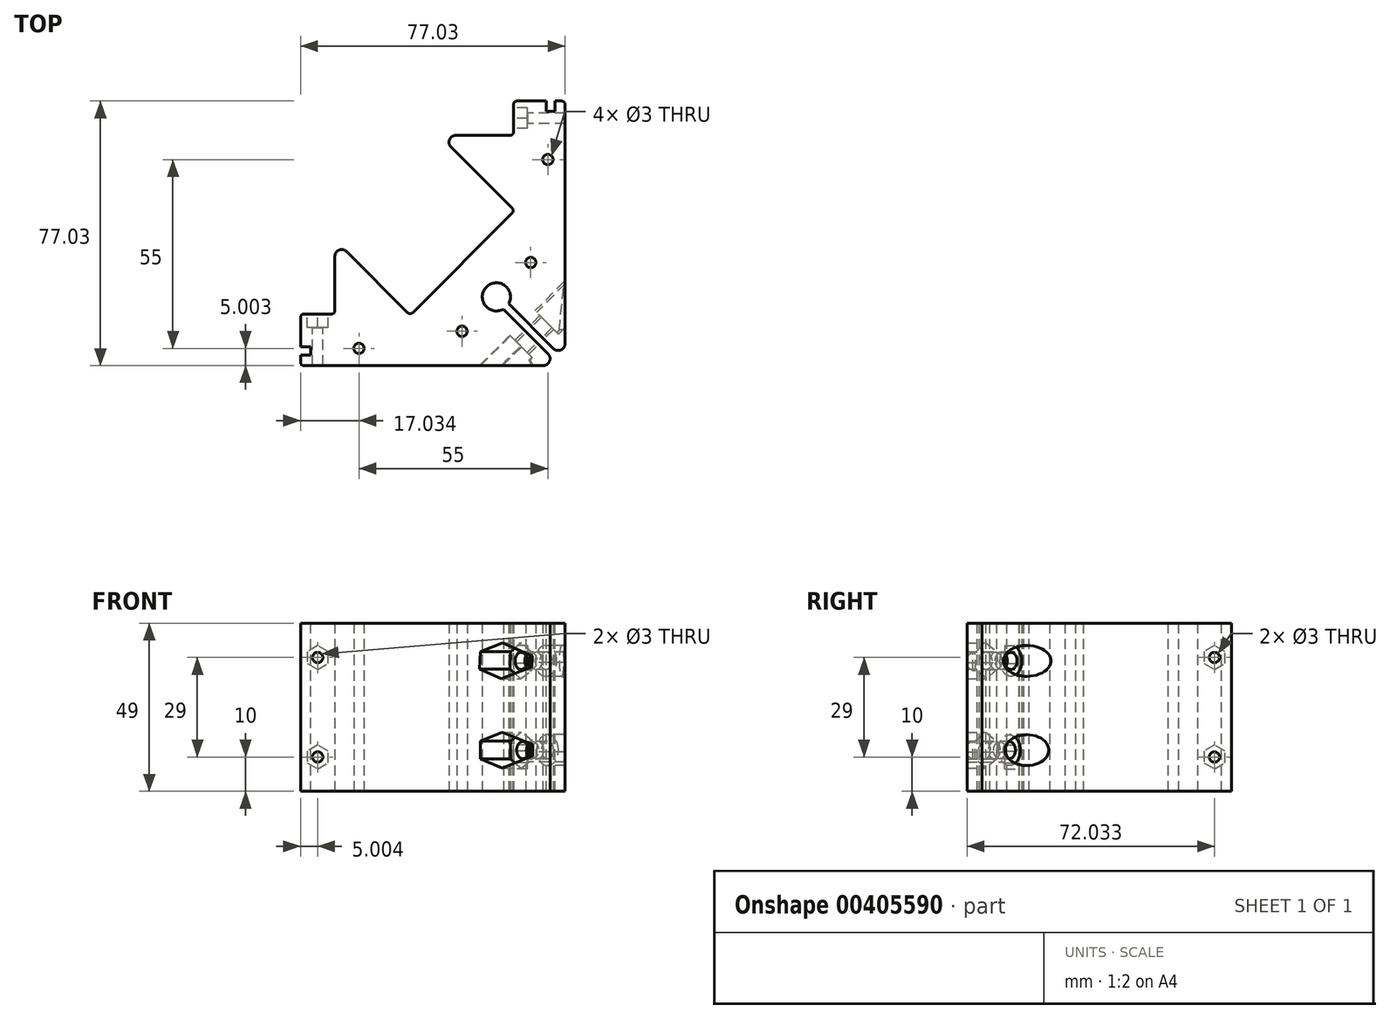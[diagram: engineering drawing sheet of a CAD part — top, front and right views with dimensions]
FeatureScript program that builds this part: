
annotation { "Feature Type Name" : "Feature", "Feature Type Description" : "" }
export const myFeature = defineFeature(function(context is Context, id is Id, definition is map)
    precondition{}
    {
        {
            var Q0;
            Q0=qCreatedBy(makeId("Top.planeOp"),FACE);
            var sketch = newSketch(context, id + "F0", { "sketchPlane" : qUnion([Q0])});
            skLineSegment(sketch, "E0.top", {"start": v(-78.82, 0.93) * mm, "end": v(-4.07, 0.93) * mm});
            skLineSegment(sketch, "E0.right", {"start": v(-1.79, 77.96) * mm, "end": v(-1.79, 3.21) * mm});
            skLineSegment(sketch, "E1", {"start": v(-18.22, 18.92) * mm, "end": v(-2.3, 3) * mm});
            skLineSegment(sketch, "E2.MirrorCS", {"start": v(-19.77, 17.36) * mm, "end": v(-3.85, 1.44) * mm});
            skPoint(sketch, "E3.visualSharp", {"position": v(-1.79, 2.49) * mm});
            skPoint(sketch, "E4.visualSharp", {"position": v(-3.34, 0.93) * mm});
            skPoint(sketch, "E5", {"position": v(-46.54, 45.68) * mm});
            skLineSegment(sketch, "E6", {"start": v(-31.69, 30.83) * mm, "end": v(-46.54, 15.98) * mm});
            skLineSegment(sketch, "E7", {"start": v(-31.69, 30.83) * mm, "end": v(-16.84, 45.68) * mm});
            skLineSegment(sketch, "E8", {"start": v(-1.79, 77.96) * mm, "end": v(-16.79, 77.96) * mm});
            skLineSegment(sketch, "E9", {"start": v(-78.82, 0.93) * mm, "end": v(-78.82, 15.93) * mm});
            skPoint(sketch, "E10.orphan", {"position": v(-49.12, 77.96) * mm});
            skLineSegment(sketch, "E11", {"start": v(-68.82, 36.93) * mm, "end": v(-68.82, 15.93) * mm});
            skLineSegment(sketch, "E12", {"start": v(-68.82, 15.93) * mm, "end": v(-78.82, 15.93) * mm});
            skLineSegment(sketch, "E13.top", {"start": v(-37.79, 67.96) * mm, "end": v(-16.79, 67.96) * mm});
            skLineSegment(sketch, "E13.right", {"start": v(-16.79, 77.96) * mm, "end": v(-16.79, 67.96) * mm});
            skArc(sketch, "E14", {"start": v(-18.22, 18.92) * mm, "mid": v(-24.69, 23.83) * mm, "end": v(-19.77, 17.36) * mm});
            skLineSegment(sketch, "E15", {"start": v(-3.85, 1.44) * mm, "end": v(-3.34, 0.93) * mm});
            skLineSegment(sketch, "E16", {"start": v(-4.07, 0.93) * mm, "end": v(-3.34, 0.93) * mm});
            skLineSegment(sketch, "E17", {"start": v(-1.79, 2.49) * mm, "end": v(-1.79, 3.21) * mm});
            skLineSegment(sketch, "E18", {"start": v(-2.3, 3) * mm, "end": v(-1.79, 2.49) * mm});
            skLineSegment(sketch, "E19", {"start": v(-46.54, 15.98) * mm, "end": v(-12.5, 50.02) * mm});
            skLineSegment(sketch, "E20", {"start": v(-16.48, 46.04) * mm, "end": v(-46.89, 15.63) * mm});
            skLineSegment(sketch, "E21", {"start": v(-16.48, 46.04) * mm, "end": v(-37.79, 67.34) * mm});
            skLineSegment(sketch, "E22", {"start": v(-46.89, 15.63) * mm, "end": v(-68.2, 36.93) * mm});
            skLineSegment(sketch, "E23", {"start": v(-68.2, 36.93) * mm, "end": v(-68.82, 37.56) * mm});
            skLineSegment(sketch, "E24", {"start": v(-68.82, 37.56) * mm, "end": v(-68.82, 36.93) * mm});
            skLineSegment(sketch, "E25", {"start": v(-37.79, 67.96) * mm, "end": v(-38.41, 67.96) * mm});
            skLineSegment(sketch, "E26", {"start": v(-37.79, 67.34) * mm, "end": v(-38.41, 67.96) * mm});
            skSolve(sketch);
        }
        {
            var Q0;
            Q0=qSketchRegion(id+"F0",true);
            extrude(context, id + "F1", {"entities" : qUnion([Q0]), "depth" : 49 * mm});
        }
        {
            var Q0;
            Q0=makeQuery(id+"F1.opExtrude","SWEPT_FACE",FACE,{"disambiguationData":[OSD([sQuery(id+"F0.wireOp",EDGE,"E1")])]});
            var sketch = newSketch(context, id + "F2", { "sketchPlane" : qUnion([Q0])});
            skCircle(sketch, "E27", {"center": v(-14.26, 12) * mm, "radius": 2.5 * mm});
            skCircle(sketch, "E28", {"center": v(-14.92, 38) * mm, "radius": 4.5 * mm});
            skCircle(sketch, "E29", {"center": v(-14.26, 12) * mm, "radius": 4.5 * mm});
            skCircle(sketch, "E30", {"center": v(-14.92, 38) * mm, "radius": 2.5 * mm});
            skCircle(sketch, "E31.cCircle", {"center": v(-14.92, 38) * mm, "radius": 4.5 * mm, "construction": true});
            skLineSegment(sketch, "E31.0", {"start": v(-10.5, 35.26) * mm, "end": v(-15.08, 32.8) * mm});
            skLineSegment(sketch, "E31.1", {"start": v(-15.08, 32.8) * mm, "end": v(-19.5, 35.54) * mm});
            skLineSegment(sketch, "E31.2", {"start": v(-19.5, 35.54) * mm, "end": v(-19.34, 40.74) * mm});
            skLineSegment(sketch, "E31.3", {"start": v(-19.34, 40.74) * mm, "end": v(-14.76, 43.2) * mm});
            skLineSegment(sketch, "E31.4", {"start": v(-14.76, 43.2) * mm, "end": v(-10.34, 40.46) * mm});
            skLineSegment(sketch, "E31.5", {"start": v(-10.34, 40.46) * mm, "end": v(-10.5, 35.26) * mm});
            skPoint(sketch, "E31.0.midPoint", {"position": v(-12.79, 34.04) * mm});
            skSolve(sketch);
        }
        {
            var Q0;
            Q0=sQuery(id+"F2.wireOp",VERTEX,"E28.center");
            var Q1;
            Q1=makeQuery(id+"F1.opExtrude","SWEPT_BODY",BODY,{"disambiguationData":[OSD([sQuery(id+"F0.wireOp",EDGE,"E0.bottom"),sQuery(id+"F0.wireOp",EDGE,"E0.top"),sQuery(id+"F0.wireOp",EDGE,"E0.left"),sQuery(id+"F0.wireOp",EDGE,"E0.right"),sQuery(id+"F0.wireOp",EDGE,"qFsGaKan-yORc-CTVH-xqod-amC7XaK1J5uG"),sQuery(id+"F0.wireOp",EDGE,"E1"),sQuery(id+"F0.wireOp",EDGE,"E2.MirrorCS"),sQuery(id+"F0.wireOp",EDGE,"cd217c19-c853-48cb-b8bd-9b78fb10cb74.filletArc"),sQuery(id+"F0.wireOp",EDGE,"a7c015ec-a513-4ea6-9d75-b2fe8166aac2.filletArc"),sQuery(id+"F0.wireOp",EDGE,"E3.filletArc"),sQuery(id+"F0.wireOp",EDGE,"E4.filletArc")])]});
            hole(context, id + "F3", {"style" : HoleStyle.SIMPLE, "endStyle" : HoleEndStyle.THROUGH, "holeDiameter" : 5 * mm, "isTappedThrough" : true, "tappedDepth" : 12 * mm, "tapClearance" : 3, "locations" : qUnion([Q0]), "scope" : qUnion([Q1])});
        }
        {
            var Q0;
            Q0=sQuery(id+"F2.wireOp",VERTEX,"E28.center");
            var Q1;
            Q1=makeQuery(id+"F1.opExtrude","SWEPT_BODY",BODY,{"disambiguationData":[OSD([sQuery(id+"F0.wireOp",EDGE,"E0.bottom"),sQuery(id+"F0.wireOp",EDGE,"E0.top"),sQuery(id+"F0.wireOp",EDGE,"E0.left"),sQuery(id+"F0.wireOp",EDGE,"E0.right"),sQuery(id+"F0.wireOp",EDGE,"qFsGaKan-yORc-CTVH-xqod-amC7XaK1J5uG"),sQuery(id+"F0.wireOp",EDGE,"E1"),sQuery(id+"F0.wireOp",EDGE,"E2.MirrorCS"),sQuery(id+"F0.wireOp",EDGE,"cd217c19-c853-48cb-b8bd-9b78fb10cb74.filletArc"),sQuery(id+"F0.wireOp",EDGE,"a7c015ec-a513-4ea6-9d75-b2fe8166aac2.filletArc"),sQuery(id+"F0.wireOp",EDGE,"E3.filletArc"),sQuery(id+"F0.wireOp",EDGE,"E4.filletArc")])]});
            hole(context, id + "F4", {"style" : HoleStyle.SIMPLE, "endStyle" : HoleEndStyle.THROUGH, "oppositeDirection" : true, "standardTappedOrClearance" : lookupTablePath({ "standard" : "自訂" }), "standardBlindInLast" : lookupTablePath({ "standard" : "自訂" }), "holeDiameter" : 5 * mm, "isTappedThrough" : true, "tappedDepth" : 12 * mm, "tapClearance" : 3, "locations" : qUnion([Q0]), "scope" : qUnion([Q1])});
        }
        {
            var Q0;
            Q0=makeQuery(id+"F2.imprint","IMPRINT",FACE,{"disambiguationData":[TD([[makeQuery(id+"F2.imprint","IMPRINT",EDGE,{"derivedFrom":sQuery(id+"F2.wireOp",EDGE,"E28")}),1.0]])]});
            var Q1;
            Q1=sQuery(id+"F2.wireOp",EDGE,"E28");
            extrude(context, id + "F5", {"entities" : qUnion([Q0]), "surfaceEntities" : qUnion([Q1]), "oppositeDirection" : true, "depth" : 25 * mm});
        }
        {
            var Q0;
            Q0=makeQuery(id+"F5.opExtrude","SWEPT_BODY",BODY,{"disambiguationData":[OSD([sQuery(id+"F2.wireOp",EDGE,"E28"),sQuery(id+"F2.wireOp",EDGE,"E30")])]});
            var Q1;
            Q1=makeQuery(id+"F1.opExtrude","SWEPT_BODY",BODY,{"disambiguationData":[OSD([sQuery(id+"F0.wireOp",EDGE,"E0.bottom"),sQuery(id+"F0.wireOp",EDGE,"E0.top"),sQuery(id+"F0.wireOp",EDGE,"E0.left"),sQuery(id+"F0.wireOp",EDGE,"E0.right"),sQuery(id+"F0.wireOp",EDGE,"qFsGaKan-yORc-CTVH-xqod-amC7XaK1J5uG"),sQuery(id+"F0.wireOp",EDGE,"E1"),sQuery(id+"F0.wireOp",EDGE,"E2.MirrorCS"),sQuery(id+"F0.wireOp",EDGE,"cd217c19-c853-48cb-b8bd-9b78fb10cb74.filletArc"),sQuery(id+"F0.wireOp",EDGE,"a7c015ec-a513-4ea6-9d75-b2fe8166aac2.filletArc"),sQuery(id+"F0.wireOp",EDGE,"E3.filletArc"),sQuery(id+"F0.wireOp",EDGE,"E4.filletArc")])]});
            booleanBodies(context, id + "F6", {"operationType" : BooleanOperationType.SUBTRACTION, "tools" : qUnion([Q0]), "targets" : qUnion([Q1])});
        }
        {
            var Q0;
            Q0=makeQuery(id+"F2.imprint","IMPRINT",FACE,{"disambiguationData":[TD([[makeQuery(id+"F2.imprint","IMPRINT",EDGE,{"derivedFrom":sQuery(id+"F2.wireOp",EDGE,"E28")}),1.0]])]});
            extrude(context, id + "F7", {"entities" : qUnion([Q0]), "operationType" : NewBodyOperationType.ADD, "oppositeDirection" : true, "depth" : 4 * mm});
        }
        {
            var Q0;
            Q0=sQuery(id+"F2.wireOp",VERTEX,"E27.center");
            var Q1;
            Q1=makeQuery(id+"F1.opExtrude","SWEPT_BODY",BODY,{"disambiguationData":[OSD([sQuery(id+"F0.wireOp",EDGE,"E0.bottom"),sQuery(id+"F0.wireOp",EDGE,"E0.top"),sQuery(id+"F0.wireOp",EDGE,"E0.left"),sQuery(id+"F0.wireOp",EDGE,"E0.right"),sQuery(id+"F0.wireOp",EDGE,"qFsGaKan-yORc-CTVH-xqod-amC7XaK1J5uG"),sQuery(id+"F0.wireOp",EDGE,"E1"),sQuery(id+"F0.wireOp",EDGE,"E2.MirrorCS"),sQuery(id+"F0.wireOp",EDGE,"cd217c19-c853-48cb-b8bd-9b78fb10cb74.filletArc"),sQuery(id+"F0.wireOp",EDGE,"a7c015ec-a513-4ea6-9d75-b2fe8166aac2.filletArc"),sQuery(id+"F0.wireOp",EDGE,"E3.filletArc"),sQuery(id+"F0.wireOp",EDGE,"E4.filletArc")])]});
            hole(context, id + "F8", {"style" : HoleStyle.SIMPLE, "endStyle" : HoleEndStyle.THROUGH, "oppositeDirection" : true, "standardTappedOrClearance" : lookupTablePath({ "standard" : "自訂" }), "standardBlindInLast" : lookupTablePath({ "standard" : "自訂" }), "holeDiameter" : 5 * mm, "isTappedThrough" : true, "tappedDepth" : 12 * mm, "tapClearance" : 3, "locations" : qUnion([Q0]), "scope" : qUnion([Q1])});
        }
        {
            var Q0;
            Q0=makeQuery(id+"F1.opExtrude","SWEPT_FACE",FACE,{"disambiguationData":[OSD([sQuery(id+"F0.wireOp",EDGE,"E2.MirrorCS")])]});
            var sketch = newSketch(context, id + "F9", { "sketchPlane" : qUnion([Q0])});
            skCircle(sketch, "E32.cCircle", {"center": v(14.92, 38) * mm, "radius": 4.5 * mm, "construction": true});
            skLineSegment(sketch, "E32.0", {"start": v(10.34, 40.45) * mm, "end": v(14.75, 43.2) * mm});
            skLineSegment(sketch, "E32.1", {"start": v(14.75, 43.2) * mm, "end": v(19.33, 40.74) * mm});
            skLineSegment(sketch, "E32.2", {"start": v(19.33, 40.74) * mm, "end": v(19.5, 35.55) * mm});
            skLineSegment(sketch, "E32.3", {"start": v(19.5, 35.55) * mm, "end": v(15.08, 32.8) * mm});
            skLineSegment(sketch, "E32.4", {"start": v(15.08, 32.8) * mm, "end": v(10.5, 35.26) * mm});
            skLineSegment(sketch, "E32.5", {"start": v(10.5, 35.26) * mm, "end": v(10.34, 40.45) * mm});
            skPoint(sketch, "E32.0.midPoint", {"position": v(12.54, 41.82) * mm});
            skCircle(sketch, "E33", {"center": v(14.92, 38) * mm, "radius": 2.5 * mm});
            skCircle(sketch, "E34.cCircle", {"center": v(14.82, 12) * mm, "radius": 4.5 * mm, "construction": true});
            skLineSegment(sketch, "E34.0", {"start": v(19.32, 14.6) * mm, "end": v(19.32, 9.4) * mm});
            skLineSegment(sketch, "E34.1", {"start": v(19.32, 9.4) * mm, "end": v(14.82, 6.8) * mm});
            skLineSegment(sketch, "E34.2", {"start": v(14.82, 6.8) * mm, "end": v(10.32, 9.4) * mm});
            skLineSegment(sketch, "E34.3", {"start": v(10.32, 9.4) * mm, "end": v(10.32, 14.6) * mm});
            skLineSegment(sketch, "E34.4", {"start": v(10.32, 14.6) * mm, "end": v(14.82, 17.2) * mm});
            skLineSegment(sketch, "E34.5", {"start": v(14.82, 17.2) * mm, "end": v(19.32, 14.6) * mm});
            skPoint(sketch, "E34.0.midPoint", {"position": v(19.32, 12) * mm});
            skSolve(sketch);
        }
        {
            var Q0;
            Q0=qSketchRegion(id+"F9",true);
            extrude(context, id + "F10", {"entities" : qUnion([Q0]), "operationType" : NewBodyOperationType.REMOVE, "oppositeDirection" : true, "depth" : 25 * mm});
        }
        {
            var Q0;
            Q0=makeQuery(id+"F9.imprint","IMPRINT",FACE,{"disambiguationData":[TD([[makeQuery(id+"F9.imprint","IMPRINT",EDGE,{"derivedFrom":sQuery(id+"F9.wireOp",EDGE,"E32.0")}),-1.0]])]});
            var Q1;
            Q1=sQuery(id+"F9.wireOp",EDGE,"E32.2");
            extrude(context, id + "F11", {"entities" : qUnion([Q0]), "operationType" : NewBodyOperationType.ADD, "surfaceEntities" : qUnion([Q1]), "oppositeDirection" : true, "depth" : 4 * mm});
        }
        {
            var Q0;
            Q0=sQuery(id+"F2.wireOp",VERTEX,"E27.center");
            var Q1;
            Q1=makeQuery(id+"F1.opExtrude","SWEPT_BODY",BODY,{"disambiguationData":[OSD([sQuery(id+"F0.wireOp",EDGE,"E0.bottom"),sQuery(id+"F0.wireOp",EDGE,"E0.top"),sQuery(id+"F0.wireOp",EDGE,"E0.left"),sQuery(id+"F0.wireOp",EDGE,"E0.right"),sQuery(id+"F0.wireOp",EDGE,"qFsGaKan-yORc-CTVH-xqod-amC7XaK1J5uG"),sQuery(id+"F0.wireOp",EDGE,"E1"),sQuery(id+"F0.wireOp",EDGE,"E2.MirrorCS"),sQuery(id+"F0.wireOp",EDGE,"cd217c19-c853-48cb-b8bd-9b78fb10cb74.filletArc"),sQuery(id+"F0.wireOp",EDGE,"a7c015ec-a513-4ea6-9d75-b2fe8166aac2.filletArc"),sQuery(id+"F0.wireOp",EDGE,"E3.filletArc"),sQuery(id+"F0.wireOp",EDGE,"E4.filletArc")])]});
            hole(context, id + "F12", {"style" : HoleStyle.SIMPLE, "endStyle" : HoleEndStyle.THROUGH, "standardTappedOrClearance" : lookupTablePath({ "standard" : "自訂" }), "standardBlindInLast" : lookupTablePath({ "standard" : "自訂" }), "holeDiameter" : 9 * mm, "isTappedThrough" : true, "tappedDepth" : 12 * mm, "tapClearance" : 3, "locations" : qUnion([Q0]), "scope" : qUnion([Q1])});
        }
        {
            var Q0;
            Q0=makeQuery(id+"F2.imprint","IMPRINT",FACE,{"disambiguationData":[TD([[makeQuery(id+"F2.imprint","IMPRINT",EDGE,{"derivedFrom":sQuery(id+"F2.wireOp",EDGE,"E27")}),-1.0]])]});
            extrude(context, id + "F13", {"entities" : qUnion([Q0]), "operationType" : NewBodyOperationType.ADD, "oppositeDirection" : true, "depth" : 4 * mm});
        }
        {
            var Q0;
            Q0=makeQuery(id+"F9.imprint","IMPRINT",FACE,{"disambiguationData":[TD([[makeQuery(id+"F9.imprint","IMPRINT",EDGE,{"derivedFrom":sQuery(id+"F9.wireOp",EDGE,"E34.0")}),-1.0]])]});
            extrude(context, id + "F14", {"entities" : qUnion([Q0]), "operationType" : NewBodyOperationType.ADD, "oppositeDirection" : true, "depth" : 4 * mm});
        }
        {
            var Q0;
            {var subQ0=sQuery(id+"F0.wireOp",EDGE,"858b2b97-0392-4feb-9a44-fc76200f76477.MirrorCS");var subQ1=sQuery(id+"F0.wireOp",EDGE,"858b2b97-0392-4feb-9a44-fc76200f76476.MirrorCS");var subQ2=sQuery(id+"F0.wireOp",EDGE,"858b2b97-0392-4feb-9a44-fc76200f76475.MirrorCS");var subQ3=sQuery(id+"F0.wireOp",EDGE,"858b2b97-0392-4feb-9a44-fc76200f76473.MirrorCS");var subQ4=sQuery(id+"F0.wireOp",EDGE,"858b2b97-0392-4feb-9a44-fc76200f76471.MirrorCS");var subQ5=sQuery(id+"F0.wireOp",EDGE,"858b2b97-0392-4feb-9a44-fc76200f76470.MirrorCS");var subQ6=sQuery(id+"F0.wireOp",EDGE,"c7b8138d-a0ca-4719-9cec-01e0daf84ff37.MirrorCS");var subQ7=sQuery(id+"F0.wireOp",EDGE,"c7b8138d-a0ca-4719-9cec-01e0daf84ff35.MirrorCS");var subQ8=sQuery(id+"F0.wireOp",EDGE,"c7b8138d-a0ca-4719-9cec-01e0daf84ff34.MirrorCS");var subQ9=sQuery(id+"F0.wireOp",EDGE,"c7b8138d-a0ca-4719-9cec-01e0daf84ff32.MirrorCS");var subQ10=sQuery(id+"F0.wireOp",EDGE,"c7b8138d-a0ca-4719-9cec-01e0daf84ff31.MirrorCS");var subQ11=sQuery(id+"F0.wireOp",EDGE,"c7b8138d-a0ca-4719-9cec-01e0daf84ff30.MirrorCS");var subQ12=sQuery(id+"F0.wireOp",EDGE,"1b5517b7-18c1-410d-9263-4c6abe080e62.5");var subQ13=sQuery(id+"F0.wireOp",EDGE,"1b5517b7-18c1-410d-9263-4c6abe080e62.4");var subQ14=sQuery(id+"F0.wireOp",EDGE,"1b5517b7-18c1-410d-9263-4c6abe080e62.3");var subQ15=sQuery(id+"F0.wireOp",EDGE,"1b5517b7-18c1-410d-9263-4c6abe080e62.2");var subQ16=sQuery(id+"F0.wireOp",EDGE,"1b5517b7-18c1-410d-9263-4c6abe080e62.1");var subQ17=sQuery(id+"F0.wireOp",EDGE,"1b5517b7-18c1-410d-9263-4c6abe080e62.0");var subQ18=sQuery(id+"F0.wireOp",EDGE,"1cc3574e-208e-4641-aa5b-36bff78b838a.5");var subQ19=sQuery(id+"F0.wireOp",EDGE,"1cc3574e-208e-4641-aa5b-36bff78b838a.4");var subQ20=sQuery(id+"F0.wireOp",EDGE,"1cc3574e-208e-4641-aa5b-36bff78b838a.3");var subQ21=sQuery(id+"F0.wireOp",EDGE,"1cc3574e-208e-4641-aa5b-36bff78b838a.2");var subQ22=sQuery(id+"F0.wireOp",EDGE,"1cc3574e-208e-4641-aa5b-36bff78b838a.1");var subQ23=sQuery(id+"F0.wireOp",EDGE,"1cc3574e-208e-4641-aa5b-36bff78b838a.0");Q0=makeQuery(id+"FfcCPochjiZxbaD_1.boolean.opBoolean","MERGE",FACE,{"derivedFrom":[makeQuery(id+"F1.opExtrude","CAP_FACE",FACE,{"disambiguationData":[OSD([sQuery(id+"F0.wireOp",EDGE,"E0.top"),sQuery(id+"F0.wireOp",EDGE,"E0.right"),sQuery(id+"F0.wireOp",EDGE,"qFsGaKan-yORc-CTVH-xqod-amC7XaK1J5uG"),sQuery(id+"F0.wireOp",EDGE,"E1"),sQuery(id+"F0.wireOp",EDGE,"E2.MirrorCS"),sQuery(id+"F0.wireOp",EDGE,"cd217c19-c853-48cb-b8bd-9b78fb10cb74.filletArc"),sQuery(id+"F0.wireOp",EDGE,"a7c015ec-a513-4ea6-9d75-b2fe8166aac2.filletArc"),sQuery(id+"F0.wireOp",EDGE,"E3.filletArc"),sQuery(id+"F0.wireOp",EDGE,"E4.filletArc"),sQuery(id+"F0.wireOp",EDGE,"IOQO6NOs-XP46-bIYv-36WW-vlzhq4IbhpyX"),sQuery(id+"F0.wireOp",EDGE,"E6"),sQuery(id+"F0.wireOp",EDGE,"E7"),sQuery(id+"F0.wireOp",EDGE,"Pufk5FBb-gGGI-5gSV-eo1E-zLzyZUmxZjv0"),sQuery(id+"F0.wireOp",EDGE,"E8"),sQuery(id+"F0.wireOp",EDGE,"E9"),sQuery(id+"F0.wireOp",EDGE,"jZstSCWU-smmE-zgHU-l8xw-nlspAIoffq16"),sQuery(id+"F0.wireOp",EDGE,"ljUfM85Z-AGBi-fIeh-n3OA-6fggT2dypjGP"),subQ23,subQ22,subQ21,subQ20,subQ19,subQ18,subQ17,subQ16,subQ15,subQ14,subQ13,subQ12,subQ11,subQ10,subQ9,subQ8,subQ7,subQ6,subQ5,subQ4,subQ3,subQ2,subQ1,subQ0])],"isStart":false}),makeQuery(id+"FfcCPochjiZxbaD_1.opExtrude","CAP_FACE",FACE,{"disambiguationData":[OSD([subQ23,subQ22,subQ21,subQ20,subQ19,subQ18,sQuery(id+"F0.wireOp",EDGE,"DxpYaAhc-Hc6j-eiyh-zj7g-wgbPevewKJgC")])],"isStart":false}),makeQuery(id+"FfcCPochjiZxbaD_1.opExtrude","CAP_FACE",FACE,{"disambiguationData":[OSD([subQ17,subQ16,subQ15,subQ14,subQ13,subQ12,sQuery(id+"F0.wireOp",EDGE,"FeovWeXt-bjZs-1ktu-chPx-rkUVs5GNt5OW")])],"isStart":false}),makeQuery(id+"FfcCPochjiZxbaD_1.opExtrude","CAP_FACE",FACE,{"disambiguationData":[OSD([subQ11,subQ10,subQ9,subQ8,subQ7,subQ6,sQuery(id+"F0.wireOp",EDGE,"c7b8138d-a0ca-4719-9cec-01e0daf84ff38.MirrorC")])],"isStart":false}),makeQuery(id+"FfcCPochjiZxbaD_1.opExtrude","CAP_FACE",FACE,{"disambiguationData":[OSD([subQ5,subQ4,subQ3,subQ2,subQ1,subQ0,sQuery(id+"F0.wireOp",EDGE,"858b2b97-0392-4feb-9a44-fc76200f76478.MirrorC")])],"isStart":false})]});}
            var sketch = newSketch(context, id + "F15", { "sketchPlane" : qUnion([Q0])});
            skLineSegment(sketch, "E35.bottom", {"start": v(-78.82, 6.43) * mm, "end": v(-75.82, 6.43) * mm});
            skLineSegment(sketch, "E35.top", {"start": v(-78.82, 3.93) * mm, "end": v(-75.82, 3.93) * mm});
            skLineSegment(sketch, "E35.left", {"start": v(-78.82, 6.43) * mm, "end": v(-78.82, 3.93) * mm});
            skLineSegment(sketch, "E35.right", {"start": v(-75.82, 6.43) * mm, "end": v(-75.82, 3.93) * mm});
            skLineSegment(sketch, "E36.bottom", {"start": v(-4.79, 77.96) * mm, "end": v(-7.29, 77.96) * mm});
            skLineSegment(sketch, "E36.top", {"start": v(-4.79, 74.96) * mm, "end": v(-7.29, 74.96) * mm});
            skLineSegment(sketch, "E36.left", {"start": v(-4.79, 77.96) * mm, "end": v(-4.79, 74.96) * mm});
            skLineSegment(sketch, "E36.right", {"start": v(-7.29, 77.96) * mm, "end": v(-7.29, 74.96) * mm});
            skSolve(sketch);
        }
        {
            var Q0;
            Q0=makeQuery(id+"F15.imprint","IMPRINT",FACE,{"disambiguationData":[TD([[makeQuery(id+"F15.imprint","IMPRINT",EDGE,{"derivedFrom":sQuery(id+"F15.wireOp",EDGE,"E36.bottom")}),1.0]])]});
            var Q1;
            Q1=makeQuery(id+"F15.imprint","IMPRINT",FACE,{"disambiguationData":[TD([[makeQuery(id+"F15.imprint","IMPRINT",EDGE,{"derivedFrom":sQuery(id+"F15.wireOp",EDGE,"E35.bottom")}),-1.0]])]});
            extrude(context, id + "F16", {"entities" : qUnion([Q0, Q1]), "operationType" : NewBodyOperationType.REMOVE, "endBound" : BoundingType.THROUGH_ALL, "oppositeDirection" : true, "depth" : 25 * mm});
        }
        {
            var Q0;
            Q0=makeQuery(id+"F1.opExtrude","SWEPT_FACE",FACE,{"disambiguationData":[OSD([sQuery(id+"F0.wireOp",EDGE,"E12")])]});
            var sketch = newSketch(context, id + "F17", { "sketchPlane" : qUnion([Q0])});
            skCircle(sketch, "E37.cCircle", {"center": v(73.82, 39) * mm, "radius": 3 * mm, "construction": true});
            skLineSegment(sketch, "E37.0", {"start": v(76.82, 40.73) * mm, "end": v(76.82, 37.27) * mm});
            skLineSegment(sketch, "E37.1", {"start": v(76.82, 37.27) * mm, "end": v(73.82, 35.54) * mm});
            skLineSegment(sketch, "E37.2", {"start": v(73.82, 35.54) * mm, "end": v(70.82, 37.27) * mm});
            skLineSegment(sketch, "E37.3", {"start": v(70.82, 37.27) * mm, "end": v(70.82, 40.73) * mm});
            skLineSegment(sketch, "E37.4", {"start": v(70.82, 40.73) * mm, "end": v(73.82, 42.46) * mm});
            skLineSegment(sketch, "E37.5", {"start": v(73.82, 42.46) * mm, "end": v(76.82, 40.73) * mm});
            skPoint(sketch, "E37.0.midPoint", {"position": v(76.82, 39) * mm});
            skCircle(sketch, "E38.cCircle", {"center": v(73.82, 10) * mm, "radius": 3 * mm, "construction": true});
            skLineSegment(sketch, "E38.0", {"start": v(76.82, 11.73) * mm, "end": v(76.82, 8.27) * mm});
            skLineSegment(sketch, "E38.1", {"start": v(76.82, 8.27) * mm, "end": v(73.82, 6.54) * mm});
            skLineSegment(sketch, "E38.2", {"start": v(73.82, 6.54) * mm, "end": v(70.82, 8.27) * mm});
            skLineSegment(sketch, "E38.3", {"start": v(70.82, 8.27) * mm, "end": v(70.82, 11.73) * mm});
            skLineSegment(sketch, "E38.4", {"start": v(70.82, 11.73) * mm, "end": v(73.82, 13.46) * mm});
            skLineSegment(sketch, "E38.5", {"start": v(73.82, 13.46) * mm, "end": v(76.82, 11.73) * mm});
            skPoint(sketch, "E38.0.midPoint", {"position": v(76.82, 10) * mm});
            skSolve(sketch);
        }
        {
            var Q0;
            Q0=qSketchRegion(id+"F17",true);
            extrude(context, id + "F18", {"entities" : qUnion([Q0]), "operationType" : NewBodyOperationType.REMOVE, "oppositeDirection" : true, "depth" : 4 * mm});
        }
        {
            var Q0;
            Q0=makeQuery(id+"F1.opExtrude","SWEPT_FACE",FACE,{"disambiguationData":[OSD([sQuery(id+"F0.wireOp",EDGE,"E13.right")])]});
            var sketch = newSketch(context, id + "F19", { "sketchPlane" : qUnion([Q0])});
            skCircle(sketch, "E39.cCircle", {"center": v(-72.96, 39) * mm, "radius": 3 * mm, "construction": true});
            skLineSegment(sketch, "E39.0", {"start": v(-75.96, 37.27) * mm, "end": v(-75.96, 40.73) * mm});
            skLineSegment(sketch, "E39.1", {"start": v(-75.96, 40.73) * mm, "end": v(-72.96, 42.46) * mm});
            skLineSegment(sketch, "E39.2", {"start": v(-72.96, 42.46) * mm, "end": v(-69.96, 40.73) * mm});
            skLineSegment(sketch, "E39.3", {"start": v(-69.96, 40.73) * mm, "end": v(-69.96, 37.27) * mm});
            skLineSegment(sketch, "E39.4", {"start": v(-69.96, 37.27) * mm, "end": v(-72.96, 35.54) * mm});
            skLineSegment(sketch, "E39.5", {"start": v(-72.96, 35.54) * mm, "end": v(-75.96, 37.27) * mm});
            skPoint(sketch, "E39.0.midPoint", {"position": v(-75.96, 39) * mm});
            skCircle(sketch, "E40.cCircle", {"center": v(-72.96, 10) * mm, "radius": 3 * mm, "construction": true});
            skLineSegment(sketch, "E40.0", {"start": v(-75.96, 8.27) * mm, "end": v(-75.96, 11.73) * mm});
            skLineSegment(sketch, "E40.1", {"start": v(-75.96, 11.73) * mm, "end": v(-72.96, 13.46) * mm});
            skLineSegment(sketch, "E40.2", {"start": v(-72.96, 13.46) * mm, "end": v(-69.96, 11.73) * mm});
            skLineSegment(sketch, "E40.3", {"start": v(-69.96, 11.73) * mm, "end": v(-69.96, 8.27) * mm});
            skLineSegment(sketch, "E40.4", {"start": v(-69.96, 8.27) * mm, "end": v(-72.96, 6.54) * mm});
            skLineSegment(sketch, "E40.5", {"start": v(-72.96, 6.54) * mm, "end": v(-75.96, 8.27) * mm});
            skPoint(sketch, "E40.0.midPoint", {"position": v(-75.96, 10) * mm});
            skSolve(sketch);
        }
        {
            var Q0;
            Q0=qSketchRegion(id+"F19",true);
            extrude(context, id + "F20", {"entities" : qUnion([Q0]), "operationType" : NewBodyOperationType.REMOVE, "oppositeDirection" : true, "depth" : 4 * mm});
        }
        {
            var Q0;
            Q0=sQuery(id+"F19.wireOp",VERTEX,"E40.cCircle.center");
            var Q1;
            Q1=sQuery(id+"F19.wireOp",VERTEX,"E39.cCircle.center");
            var Q2;
            Q2=sQuery(id+"F17.wireOp",VERTEX,"E37.cCircle.center");
            var Q3;
            Q3=sQuery(id+"F17.wireOp",VERTEX,"E38.cCircle.center");
            var Q4;
            Q4=makeQuery(id+"F1.opExtrude","SWEPT_BODY",BODY,{"disambiguationData":[OSD([sQuery(id+"F0.wireOp",EDGE,"E0.top"),sQuery(id+"F0.wireOp",EDGE,"E0.right"),sQuery(id+"F0.wireOp",EDGE,"qFsGaKan-yORc-CTVH-xqod-amC7XaK1J5uG"),sQuery(id+"F0.wireOp",EDGE,"E1"),sQuery(id+"F0.wireOp",EDGE,"E2.MirrorCS"),sQuery(id+"F0.wireOp",EDGE,"cd217c19-c853-48cb-b8bd-9b78fb10cb74.filletArc"),sQuery(id+"F0.wireOp",EDGE,"a7c015ec-a513-4ea6-9d75-b2fe8166aac2.filletArc"),sQuery(id+"F0.wireOp",EDGE,"E3.filletArc"),sQuery(id+"F0.wireOp",EDGE,"E4.filletArc"),sQuery(id+"F0.wireOp",EDGE,"IOQO6NOs-XP46-bIYv-36WW-vlzhq4IbhpyX"),sQuery(id+"F0.wireOp",EDGE,"E6"),sQuery(id+"F0.wireOp",EDGE,"E7"),sQuery(id+"F0.wireOp",EDGE,"Pufk5FBb-gGGI-5gSV-eo1E-zLzyZUmxZjv0"),sQuery(id+"F0.wireOp",EDGE,"E8"),sQuery(id+"F0.wireOp",EDGE,"E9"),sQuery(id+"F0.wireOp",EDGE,"jZstSCWU-smmE-zgHU-l8xw-nlspAIoffq16"),sQuery(id+"F0.wireOp",EDGE,"ljUfM85Z-AGBi-fIeh-n3OA-6fggT2dypjGP"),sQuery(id+"F0.wireOp",EDGE,"1cc3574e-208e-4641-aa5b-36bff78b838a.0"),sQuery(id+"F0.wireOp",EDGE,"1cc3574e-208e-4641-aa5b-36bff78b838a.1"),sQuery(id+"F0.wireOp",EDGE,"1cc3574e-208e-4641-aa5b-36bff78b838a.2"),sQuery(id+"F0.wireOp",EDGE,"1cc3574e-208e-4641-aa5b-36bff78b838a.3"),sQuery(id+"F0.wireOp",EDGE,"1cc3574e-208e-4641-aa5b-36bff78b838a.4"),sQuery(id+"F0.wireOp",EDGE,"1cc3574e-208e-4641-aa5b-36bff78b838a.5"),sQuery(id+"F0.wireOp",EDGE,"1b5517b7-18c1-410d-9263-4c6abe080e62.0"),sQuery(id+"F0.wireOp",EDGE,"1b5517b7-18c1-410d-9263-4c6abe080e62.1"),sQuery(id+"F0.wireOp",EDGE,"1b5517b7-18c1-410d-9263-4c6abe080e62.2"),sQuery(id+"F0.wireOp",EDGE,"1b5517b7-18c1-410d-9263-4c6abe080e62.3"),sQuery(id+"F0.wireOp",EDGE,"1b5517b7-18c1-410d-9263-4c6abe080e62.4"),sQuery(id+"F0.wireOp",EDGE,"1b5517b7-18c1-410d-9263-4c6abe080e62.5"),sQuery(id+"F0.wireOp",EDGE,"c7b8138d-a0ca-4719-9cec-01e0daf84ff30.MirrorCS"),sQuery(id+"F0.wireOp",EDGE,"c7b8138d-a0ca-4719-9cec-01e0daf84ff31.MirrorCS"),sQuery(id+"F0.wireOp",EDGE,"c7b8138d-a0ca-4719-9cec-01e0daf84ff32.MirrorCS"),sQuery(id+"F0.wireOp",EDGE,"c7b8138d-a0ca-4719-9cec-01e0daf84ff34.MirrorCS"),sQuery(id+"F0.wireOp",EDGE,"c7b8138d-a0ca-4719-9cec-01e0daf84ff35.MirrorCS"),sQuery(id+"F0.wireOp",EDGE,"c7b8138d-a0ca-4719-9cec-01e0daf84ff37.MirrorCS"),sQuery(id+"F0.wireOp",EDGE,"858b2b97-0392-4feb-9a44-fc76200f76470.MirrorCS"),sQuery(id+"F0.wireOp",EDGE,"858b2b97-0392-4feb-9a44-fc76200f76471.MirrorCS"),sQuery(id+"F0.wireOp",EDGE,"858b2b97-0392-4feb-9a44-fc76200f76473.MirrorCS"),sQuery(id+"F0.wireOp",EDGE,"858b2b97-0392-4feb-9a44-fc76200f76475.MirrorCS"),sQuery(id+"F0.wireOp",EDGE,"858b2b97-0392-4feb-9a44-fc76200f76476.MirrorCS"),sQuery(id+"F0.wireOp",EDGE,"858b2b97-0392-4feb-9a44-fc76200f76477.MirrorCS"),sQuery(id+"F0.wireOp",EDGE,"E11"),sQuery(id+"F0.wireOp",EDGE,"E12"),sQuery(id+"F0.wireOp",EDGE,"E13.top"),sQuery(id+"F0.wireOp",EDGE,"E13.right")])]});
            hole(context, id + "F21", {"style" : HoleStyle.SIMPLE, "endStyle" : HoleEndStyle.THROUGH, "holeDiameter" : 3 * mm, "isTappedThrough" : true, "tappedDepth" : 12 * mm, "tapClearance" : 3, "locations" : qUnion([Q0, Q1, Q2, Q3]), "scope" : qUnion([Q4])});
        }
        {
            var Q0;
            Q0=makeQuery(id+"F1.opExtrude","SWEPT_EDGE",EDGE,{"disambiguationData":[OSD([sQuery(id+"F0.wireOp",EDGE,"E11"),sQuery(id+"F0.wireOp",EDGE,"E12")])]});
            var Q1;
            Q1=makeQuery(id+"F1.opExtrude","SWEPT_EDGE",EDGE,{"disambiguationData":[OSD([sQuery(id+"F0.wireOp",EDGE,"E13.top"),sQuery(id+"F0.wireOp",EDGE,"E13.right")])]});
            var Q2;
            Q2=makeQuery(id+"F1.opExtrude","SWEPT_EDGE",EDGE,{"disambiguationData":[OSD([sQuery(id+"F0.wireOp",EDGE,"E0.right"),sQuery(id+"F0.wireOp",EDGE,"E8")])]});
            var Q3;
            Q3=makeQuery(id+"F1.opExtrude","SWEPT_EDGE",EDGE,{"disambiguationData":[OSD([sQuery(id+"F0.wireOp",EDGE,"E0.top"),sQuery(id+"F0.wireOp",EDGE,"E9")])]});
            var Q4;
            Q4=makeQuery(id+"F1.opExtrude","SWEPT_EDGE",EDGE,{"disambiguationData":[OSD([sQuery(id+"F0.wireOp",EDGE,"E8"),sQuery(id+"F0.wireOp",EDGE,"E13.right")])]});
            var Q5;
            Q5=makeQuery(id+"F1.opExtrude","SWEPT_EDGE",EDGE,{"disambiguationData":[OSD([sQuery(id+"F0.wireOp",EDGE,"E9"),sQuery(id+"F0.wireOp",EDGE,"E12")])]});
            var Q6;
            Q6=makeQuery(id+"F21.hole-2.boolean.opBoolean","INTERSECT",EDGE,{"derivedFrom":[makeQuery(id+"F1.opExtrude","SWEPT_FACE",FACE,{"disambiguationData":[OSD([sQuery(id+"F0.wireOp",EDGE,"E0.top")])]}),makeQuery(id+"F21.hole-2.opRevolve","SWEPT_FACE",FACE,{"disambiguationData":[OSD([sQuery(id+"F21.hole-2.sketch.wireOp",EDGE,"core_line_2")])]})]});
            var Q7;
            Q7=makeQuery(id+"F21.hole-3.boolean.opBoolean","INTERSECT",EDGE,{"derivedFrom":[makeQuery(id+"F1.opExtrude","SWEPT_FACE",FACE,{"disambiguationData":[OSD([sQuery(id+"F0.wireOp",EDGE,"E0.top")])]}),makeQuery(id+"F21.hole-3.opRevolve","SWEPT_FACE",FACE,{"disambiguationData":[OSD([sQuery(id+"F21.hole-3.sketch.wireOp",EDGE,"core_line_2")])]})]});
            var Q8;
            Q8=makeQuery(id+"F12.hole-0.boolean.opBoolean","INTERSECT",EDGE,{"derivedFrom":[makeQuery(id+"F1.opExtrude","SWEPT_FACE",FACE,{"disambiguationData":[OSD([sQuery(id+"F0.wireOp",EDGE,"E0.right")])]}),makeQuery(id+"F12.hole-0.opRevolve","SWEPT_FACE",FACE,{"disambiguationData":[OSD([sQuery(id+"F12.hole-0.sketch.wireOp",EDGE,"core_line_2")])]})]});
            var Q9;
            Q9=makeQuery(id+"F6.opBoolean","INTERSECT",EDGE,{"derivedFrom":[makeQuery(id+"F1.opExtrude","SWEPT_FACE",FACE,{"disambiguationData":[OSD([sQuery(id+"F0.wireOp",EDGE,"E0.right")])]}),makeQuery(id+"F5.opExtrude","SWEPT_FACE",FACE,{"disambiguationData":[OSD([sQuery(id+"F2.wireOp",EDGE,"E28")])]})]});
            var Q10;
            Q10=makeQuery(id+"F21.hole-0.boolean.opBoolean","INTERSECT",EDGE,{"derivedFrom":[makeQuery(id+"F1.opExtrude","SWEPT_FACE",FACE,{"disambiguationData":[OSD([sQuery(id+"F0.wireOp",EDGE,"E0.right")])]}),makeQuery(id+"F21.hole-0.opRevolve","SWEPT_FACE",FACE,{"disambiguationData":[OSD([sQuery(id+"F21.hole-0.sketch.wireOp",EDGE,"core_line_2")])]})]});
            var Q11;
            Q11=makeQuery(id+"F21.hole-1.boolean.opBoolean","INTERSECT",EDGE,{"derivedFrom":[makeQuery(id+"F1.opExtrude","SWEPT_FACE",FACE,{"disambiguationData":[OSD([sQuery(id+"F0.wireOp",EDGE,"E0.right")])]}),makeQuery(id+"F21.hole-1.opRevolve","SWEPT_FACE",FACE,{"disambiguationData":[OSD([sQuery(id+"F21.hole-1.sketch.wireOp",EDGE,"core_line_2")])]})]});
            fillet(context, id + "F22", {"entities" : qUnion([Q0, Q1, Q2, Q3, Q4, Q5, Q6, Q7, Q8, Q9, Q10, Q11]), "radius" : 1 * mm, "tangentPropagation" : true, "allowEdgeOverflow" : false});
        }
        {
            var Q0;
            Q0=makeQuery(id+"F10.boolean.opBoolean","INTERSECT",EDGE,{"derivedFrom":[makeQuery(id+"F1.opExtrude","SWEPT_FACE",FACE,{"disambiguationData":[OSD([sQuery(id+"F0.wireOp",EDGE,"E0.top")])]}),makeQuery(id+"F10.opExtrude","SWEPT_FACE",FACE,{"disambiguationData":[OSD([sQuery(id+"F9.wireOp",EDGE,"E34.3")])]})]});
            var Q1;
            Q1=makeQuery(id+"F10.boolean.opBoolean","INTERSECT",EDGE,{"derivedFrom":[makeQuery(id+"F1.opExtrude","SWEPT_FACE",FACE,{"disambiguationData":[OSD([sQuery(id+"F0.wireOp",EDGE,"E0.top")])]}),makeQuery(id+"F10.opExtrude","SWEPT_FACE",FACE,{"disambiguationData":[OSD([sQuery(id+"F9.wireOp",EDGE,"E32.5")])]})]});
            chamfer(context, id + "F23", {"entities" : qUnion([Q0, Q1]), "width" : 1 * mm, "tangentPropagation" : true});
        }
        {
            var Q0;
            Q0=makeQuery(id+"F1.opExtrude","SWEPT_EDGE",EDGE,{"disambiguationData":[OSD([sQuery(id+"F0.wireOp",EDGE,"E15"),sQuery(id+"F0.wireOp",EDGE,"E16")])]});
            var Q1;
            Q1=makeQuery(id+"F1.opExtrude","SWEPT_EDGE",EDGE,{"disambiguationData":[OSD([sQuery(id+"F0.wireOp",EDGE,"E17"),sQuery(id+"F0.wireOp",EDGE,"E18")])]});
            fillet(context, id + "F24", {"entities" : qUnion([Q0, Q1]), "radius" : 2 * mm, "tangentPropagation" : true, "allowEdgeOverflow" : false});
        }
        {
            var Q0;
            Q0=makeQuery(id+"F1.opExtrude","SWEPT_EDGE",EDGE,{"disambiguationData":[OSD([sQuery(id+"F0.wireOp",EDGE,"E23"),sQuery(id+"F0.wireOp",EDGE,"E24")])]});
            var Q1;
            Q1=makeQuery(id+"F1.opExtrude","SWEPT_EDGE",EDGE,{"disambiguationData":[OSD([sQuery(id+"F0.wireOp",EDGE,"E25"),sQuery(id+"F0.wireOp",EDGE,"E26")])]});
            fillet(context, id + "F25", {"entities" : qUnion([Q0, Q1]), "radius" : 2 * mm, "tangentPropagation" : true, "allowEdgeOverflow" : false});
        }
        {
            var Q0;
            Q0=makeQuery(id+"F1.opExtrude","SWEPT_EDGE",EDGE,{"disambiguationData":[OSD([sQuery(id+"F0.wireOp",EDGE,"E20"),sQuery(id+"F0.wireOp",EDGE,"E21")])]});
            var Q1;
            Q1=makeQuery(id+"F1.opExtrude","SWEPT_EDGE",EDGE,{"disambiguationData":[OSD([sQuery(id+"F0.wireOp",EDGE,"E20"),sQuery(id+"F0.wireOp",EDGE,"E22")])]});
            fillet(context, id + "F26", {"entities" : qUnion([Q0, Q1]), "radius" : 1 * mm, "tangentPropagation" : true, "allowEdgeOverflow" : false});
        }
        {
            var Q0;
            Q0=makeQuery(id+"F1.opExtrude","CAP_FACE",FACE,{"disambiguationData":[OSD([sQuery(id+"F0.wireOp",EDGE,"E0.top"),sQuery(id+"F0.wireOp",EDGE,"E0.right"),sQuery(id+"F0.wireOp",EDGE,"E1"),sQuery(id+"F0.wireOp",EDGE,"E2.MirrorCS"),sQuery(id+"F0.wireOp",EDGE,"E8"),sQuery(id+"F0.wireOp",EDGE,"E9"),sQuery(id+"F0.wireOp",EDGE,"E11"),sQuery(id+"F0.wireOp",EDGE,"E12"),sQuery(id+"F0.wireOp",EDGE,"E13.top"),sQuery(id+"F0.wireOp",EDGE,"E13.right"),sQuery(id+"F0.wireOp",EDGE,"E14"),sQuery(id+"F0.wireOp",EDGE,"E15"),sQuery(id+"F0.wireOp",EDGE,"E16"),sQuery(id+"F0.wireOp",EDGE,"E17"),sQuery(id+"F0.wireOp",EDGE,"E18"),sQuery(id+"F0.wireOp",EDGE,"E20"),sQuery(id+"F0.wireOp",EDGE,"E21"),sQuery(id+"F0.wireOp",EDGE,"E22"),sQuery(id+"F0.wireOp",EDGE,"E23"),sQuery(id+"F0.wireOp",EDGE,"E24"),sQuery(id+"F0.wireOp",EDGE,"E25"),sQuery(id+"F0.wireOp",EDGE,"E26")])],"isStart":true});
            var sketch = newSketch(context, id + "F27", { "sketchPlane" : qUnion([Q0])});
            skCircle(sketch, "E41", {"center": v(-11.79, -30.93) * mm, "radius": 2.8 * mm});
            skCircle(sketch, "E42", {"center": v(-6.79, -60.93) * mm, "radius": 2.65 * mm});
            skCircle(sketch, "E43", {"center": v(-31.79, -10.93) * mm, "radius": 2.87 * mm});
            skCircle(sketch, "E44", {"center": v(-61.79, -5.93) * mm, "radius": 2.52 * mm});
            skLineSegment(sketch, "E45", {"start": v(-1.79, -22.73) * mm, "end": v(-1.79, -34.37) * mm});
            skLineSegment(sketch, "E46", {"start": v(-70.96, -0.93) * mm, "end": v(-43, -0.93) * mm});
            skSolve(sketch);
        }
        {
            var Q0;
            Q0=sQuery(id+"F27.wireOp",VERTEX,"E44.center");
            var Q1;
            Q1=sQuery(id+"F27.wireOp",VERTEX,"E43.center");
            var Q2;
            Q2=sQuery(id+"F27.wireOp",VERTEX,"E41.center");
            var Q3;
            Q3=sQuery(id+"F27.wireOp",VERTEX,"E42.center");
            var Q4;
            Q4=makeQuery(id+"F1.opExtrude","SWEPT_BODY",BODY,{"disambiguationData":[OSD([sQuery(id+"F0.wireOp",EDGE,"E0.top"),sQuery(id+"F0.wireOp",EDGE,"E0.right"),sQuery(id+"F0.wireOp",EDGE,"E1"),sQuery(id+"F0.wireOp",EDGE,"E2.MirrorCS"),sQuery(id+"F0.wireOp",EDGE,"E8"),sQuery(id+"F0.wireOp",EDGE,"E9"),sQuery(id+"F0.wireOp",EDGE,"E11"),sQuery(id+"F0.wireOp",EDGE,"E12"),sQuery(id+"F0.wireOp",EDGE,"E13.top"),sQuery(id+"F0.wireOp",EDGE,"E13.right"),sQuery(id+"F0.wireOp",EDGE,"E14"),sQuery(id+"F0.wireOp",EDGE,"E15"),sQuery(id+"F0.wireOp",EDGE,"E16"),sQuery(id+"F0.wireOp",EDGE,"E17"),sQuery(id+"F0.wireOp",EDGE,"E18"),sQuery(id+"F0.wireOp",EDGE,"E20"),sQuery(id+"F0.wireOp",EDGE,"E21"),sQuery(id+"F0.wireOp",EDGE,"E22"),sQuery(id+"F0.wireOp",EDGE,"E23"),sQuery(id+"F0.wireOp",EDGE,"E24"),sQuery(id+"F0.wireOp",EDGE,"E25"),sQuery(id+"F0.wireOp",EDGE,"E26")])]});
            hole(context, id + "F28", {"style" : HoleStyle.SIMPLE, "endStyle" : HoleEndStyle.THROUGH, "holeDiameter" : 3 * mm, "isTappedThrough" : true, "tappedDepth" : 12 * mm, "tapClearance" : 3, "locations" : qUnion([Q0, Q1, Q2, Q3]), "scope" : qUnion([Q4])});
        }
    });
